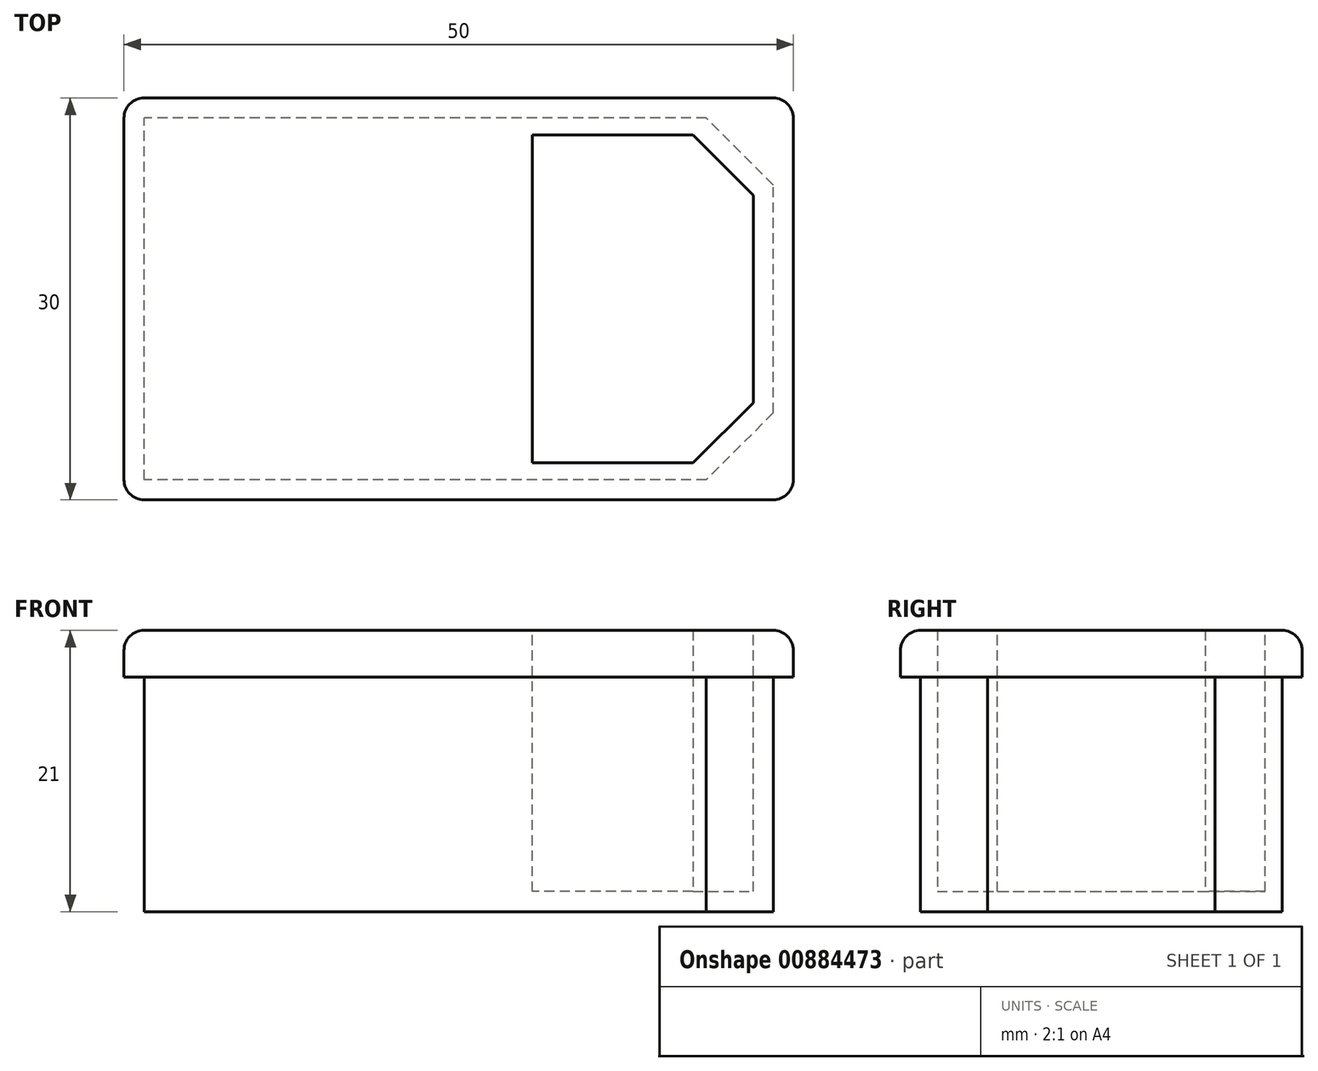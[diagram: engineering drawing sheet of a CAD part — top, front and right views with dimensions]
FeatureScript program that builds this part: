
annotation { "Feature Type Name" : "Feature", "Feature Type Description" : "" }
export const myFeature = defineFeature(function(context is Context, id is Id, definition is map)
    precondition{}
    {
        {
            var Q0;
            Q0=qCreatedBy(makeId("Top.planeOp"),FACE);
            var sketch = newSketch(context, id + "F0", { "sketchPlane" : qUnion([Q0])});
            skLineSegment(sketch, "E0.bottom", {"start": v(23.5, -13.5) * mm, "end": v(-23.5, -13.5) * mm});
            skLineSegment(sketch, "E0.top", {"start": v(23.5, 13.5) * mm, "end": v(-23.5, 13.5) * mm});
            skLineSegment(sketch, "E0.left", {"start": v(23.5, -13.5) * mm, "end": v(23.5, 13.5) * mm});
            skLineSegment(sketch, "E0.right", {"start": v(-23.5, -13.5) * mm, "end": v(-23.5, 13.5) * mm});
            skPoint(sketch, "E0.middle", {"position": v(0, 0) * mm});
            skLineSegment(sketch, "E1.0", {"start": v(25, 15) * mm, "end": v(-25, 15) * mm});
            skLineSegment(sketch, "E1.1", {"start": v(25, -15) * mm, "end": v(25, 15) * mm});
            skLineSegment(sketch, "E1.2", {"start": v(25, -15) * mm, "end": v(-25, -15) * mm});
            skLineSegment(sketch, "E1.3", {"start": v(-25, -15) * mm, "end": v(-25, 15) * mm});
            skSolve(sketch);
        }
        {
            var Q0;
            Q0=makeQuery(id+"F0.imprint","IMPRINT",FACE,{"disambiguationData":[TD([[makeQuery(id+"F0.imprint","IMPRINT",EDGE,{"derivedFrom":sQuery(id+"F0.wireOp",EDGE,"E0.bottom")}),-1.0]])]});
            extrude(context, id + "F1", {"entities" : qUnion([Q0]), "oppositeDirection" : true, "depth" : 17.5 * mm, "offsetDistance" : 25 * mm});
        }
        {
            var Q0;
            Q0=makeQuery(id+"F0.imprint","IMPRINT",FACE,{"disambiguationData":[TD([[makeQuery(id+"F0.imprint","IMPRINT",EDGE,{"derivedFrom":sQuery(id+"F0.wireOp",EDGE,"E0.bottom")}),1.0]])]});
            var Q1;
            Q1=makeQuery(id+"F0.imprint","IMPRINT",FACE,{"disambiguationData":[TD([[makeQuery(id+"F0.imprint","IMPRINT",EDGE,{"derivedFrom":sQuery(id+"F0.wireOp",EDGE,"E0.bottom")}),-1.0]])]});
            extrude(context, id + "F2", {"entities" : qUnion([Q0, Q1]), "operationType" : NewBodyOperationType.ADD, "depth" : 3.5 * mm, "offsetDistance" : 25 * mm});
        }
        {
            var Q0;
            Q0=makeQuery(id+"F2.opExtrude","CAP_FACE",FACE,{"disambiguationData":[OSD([sQuery(id+"F0.wireOp",EDGE,"E1.0"),sQuery(id+"F0.wireOp",EDGE,"E1.1"),sQuery(id+"F0.wireOp",EDGE,"E1.2"),sQuery(id+"F0.wireOp",EDGE,"E1.3")])],"isStart":false});
            var sketch = newSketch(context, id + "F3", { "sketchPlane" : qUnion([Q0])});
            skLineSegment(sketch, "E2", {"start": v(25, 0) * mm, "end": v(-25, 0) * mm, "construction": true});
            skLineSegment(sketch, "E3.bottom", {"start": v(22, -12.25) * mm, "end": v(5.5, -12.25) * mm});
            skLineSegment(sketch, "E3.top", {"start": v(22, 12.25) * mm, "end": v(5.5, 12.25) * mm});
            skLineSegment(sketch, "E3.left", {"start": v(22, -12.25) * mm, "end": v(22, 12.25) * mm});
            skLineSegment(sketch, "E3.right", {"start": v(5.5, -12.25) * mm, "end": v(5.5, 12.25) * mm});
            skPoint(sketch, "E3.middle", {"position": v(13.75, 0) * mm});
            skSolve(sketch);
        }
        {
            var Q0;
            Q0=makeQuery(id+"F3.imprint","IMPRINT",FACE,{"disambiguationData":[TD([[makeQuery(id+"F3.imprint","IMPRINT",EDGE,{"derivedFrom":sQuery(id+"F3.wireOp",EDGE,"E3.bottom")}),-1.0]])]});
            extrude(context, id + "F4", {"entities" : qUnion([Q0]), "operationType" : NewBodyOperationType.REMOVE, "oppositeDirection" : true, "depth" : 19.5 * mm, "offsetDistance" : 25 * mm});
        }
        {
            var Q0;
            Q0=makeQuery(id+"F4.boolean.opBoolean","COPY",EDGE,{"derivedFrom":makeQuery(id+"F4.opExtrude","SWEPT_EDGE",EDGE,{"disambiguationData":[OSD([sQuery(id+"F3.wireOp",EDGE,"E3.top"),sQuery(id+"F3.wireOp",EDGE,"E3.left")])]})});
            var Q1;
            Q1=makeQuery(id+"F4.boolean.opBoolean","COPY",EDGE,{"derivedFrom":makeQuery(id+"F4.opExtrude","SWEPT_EDGE",EDGE,{"disambiguationData":[OSD([sQuery(id+"F3.wireOp",EDGE,"E3.bottom"),sQuery(id+"F3.wireOp",EDGE,"E3.left")])]})});
            chamfer(context, id + "F5", {"entities" : qUnion([Q0, Q1]), "width" : 4.5 * mm, "tangentPropagation" : true});
        }
        {
            var Q0;
            Q0=makeQuery(id+"F1.opExtrude","SWEPT_EDGE",EDGE,{"disambiguationData":[OSD([sQuery(id+"F0.wireOp",EDGE,"E0.top"),sQuery(id+"F0.wireOp",EDGE,"E0.left")])]});
            var Q1;
            Q1=makeQuery(id+"F1.opExtrude","SWEPT_EDGE",EDGE,{"disambiguationData":[OSD([sQuery(id+"F0.wireOp",EDGE,"E0.bottom"),sQuery(id+"F0.wireOp",EDGE,"E0.left")])]});
            chamfer(context, id + "F6", {"entities" : qUnion([Q0, Q1]), "width" : 5 * mm, "tangentPropagation" : true});
        }
        {
            var Q0;
            Q0=makeQuery(id+"F2.opExtrude","CAP_EDGE",EDGE,{"disambiguationData":[OSD([sQuery(id+"F0.wireOp",EDGE,"E1.3")])],"isStart":false});
            var Q1;
            Q1=makeQuery(id+"F2.opExtrude","CAP_EDGE",EDGE,{"disambiguationData":[OSD([sQuery(id+"F0.wireOp",EDGE,"E1.0")])],"isStart":false});
            var Q2;
            Q2=makeQuery(id+"F2.opExtrude","CAP_EDGE",EDGE,{"disambiguationData":[OSD([sQuery(id+"F0.wireOp",EDGE,"E1.1")])],"isStart":false});
            var Q3;
            Q3=makeQuery(id+"F2.opExtrude","CAP_EDGE",EDGE,{"disambiguationData":[OSD([sQuery(id+"F0.wireOp",EDGE,"E1.2")])],"isStart":false});
            var Q4;
            Q4=makeQuery(id+"F2.opExtrude","SWEPT_EDGE",EDGE,{"disambiguationData":[OSD([sQuery(id+"F0.wireOp",EDGE,"E1.1"),sQuery(id+"F0.wireOp",EDGE,"E1.2")])]});
            var Q5;
            Q5=makeQuery(id+"F2.opExtrude","SWEPT_EDGE",EDGE,{"disambiguationData":[OSD([sQuery(id+"F0.wireOp",EDGE,"E1.0"),sQuery(id+"F0.wireOp",EDGE,"E1.1")])]});
            var Q6;
            Q6=makeQuery(id+"F2.opExtrude","SWEPT_EDGE",EDGE,{"disambiguationData":[OSD([sQuery(id+"F0.wireOp",EDGE,"E1.2"),sQuery(id+"F0.wireOp",EDGE,"E1.3")])]});
            var Q7;
            Q7=makeQuery(id+"F2.opExtrude","SWEPT_EDGE",EDGE,{"disambiguationData":[OSD([sQuery(id+"F0.wireOp",EDGE,"E1.0"),sQuery(id+"F0.wireOp",EDGE,"E1.3")])]});
            fillet(context, id + "F7", {"entities" : qUnion([Q0, Q1, Q2, Q3, Q4, Q5, Q6, Q7]), "radius" : 1.5 * mm, "tangentPropagation" : true, "allowEdgeOverflow" : false});
        }
    });
